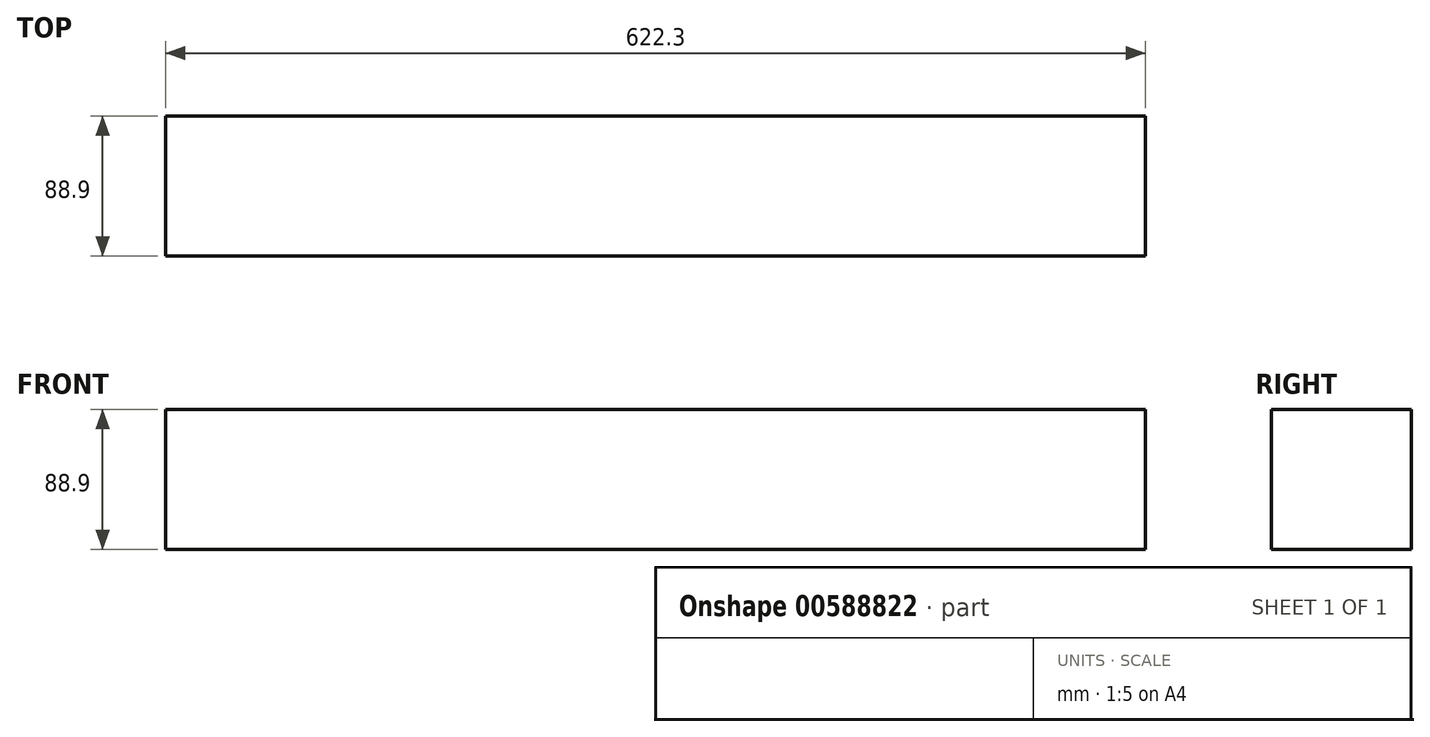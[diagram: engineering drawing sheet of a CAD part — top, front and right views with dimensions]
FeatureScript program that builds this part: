
annotation { "Feature Type Name" : "Feature", "Feature Type Description" : "" }
export const myFeature = defineFeature(function(context is Context, id is Id, definition is map)
    precondition{}
    {
        {
            var Q0;
            Q0=qCreatedBy(makeId("Right.planeOp"),FACE);
            var sketch = newSketch(context, id + "F0", { "sketchPlane" : qUnion([Q0])});
            skLineSegment(sketch, "E0.bottom", {"start": v(0, 0) * mm, "end": v(88.9, 0) * mm});
            skLineSegment(sketch, "E0.top", {"start": v(0, 88.9) * mm, "end": v(88.9, 88.9) * mm});
            skLineSegment(sketch, "E0.left", {"start": v(0, 0) * mm, "end": v(0, 88.9) * mm});
            skLineSegment(sketch, "E0.right", {"start": v(88.9, 0) * mm, "end": v(88.9, 88.9) * mm});
            skSolve(sketch);
        }
        {
            var Q0;
            Q0=makeQuery(id+"F0.imprint","IMPRINT",FACE,{"disambiguationData":[TD([[makeQuery(id+"F0.imprint","IMPRINT",EDGE,{"derivedFrom":sQuery(id+"F0.wireOp",EDGE,"E0.bottom")}),1.0]])]});
            extrude(context, id + "F1", {"entities" : qUnion([Q0]), "oppositeDirection" : true, "depth" : 622.3 * mm, "offsetDistance" : 25.4 * mm});
        }
    });
